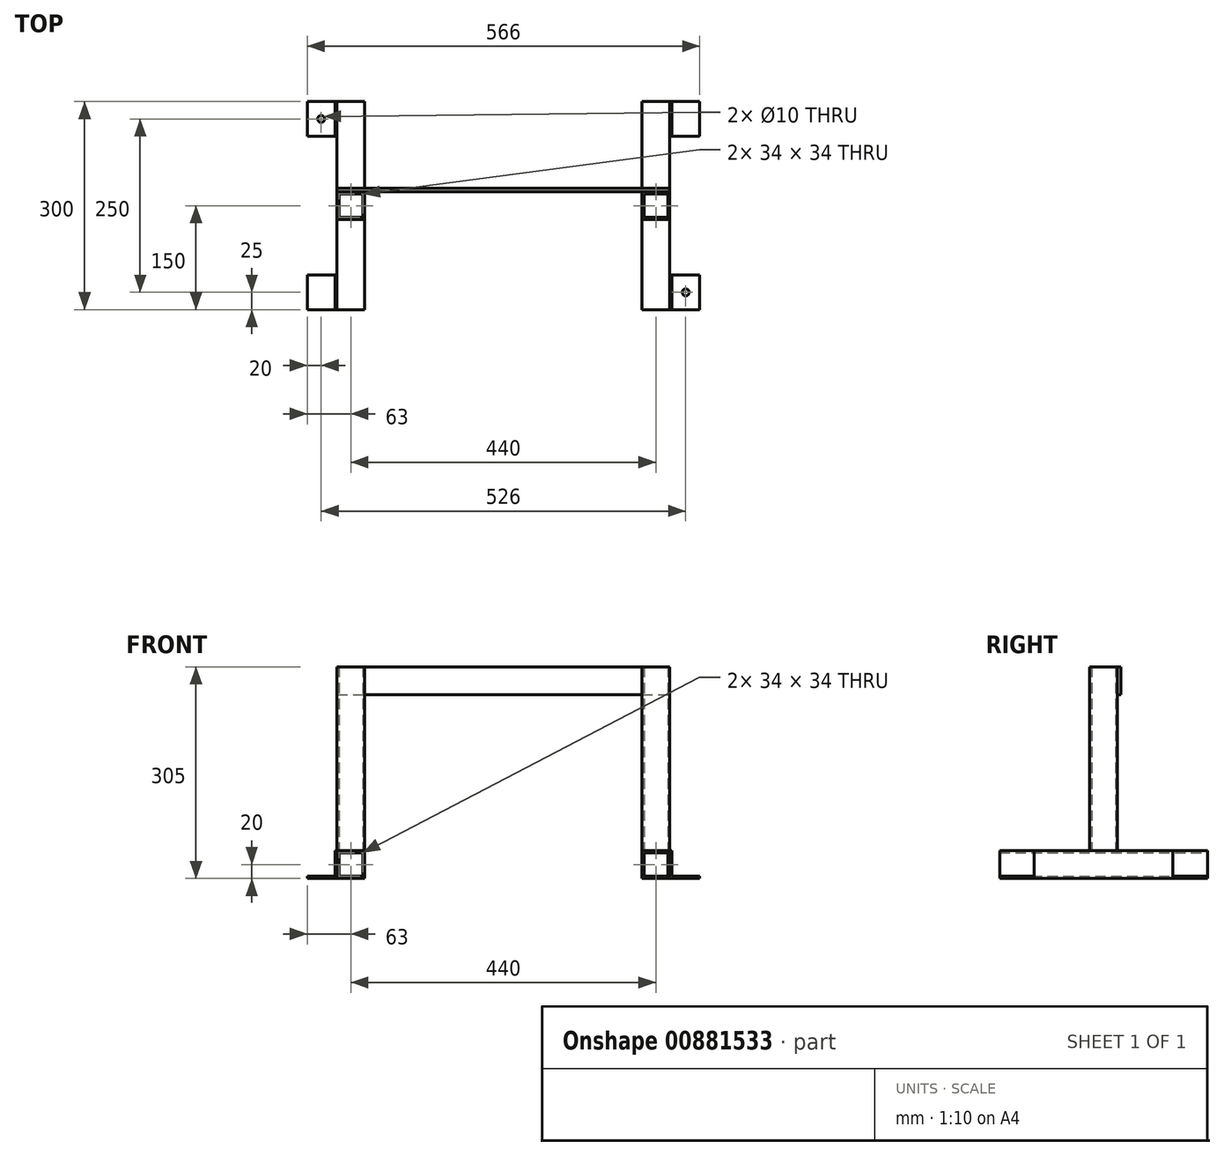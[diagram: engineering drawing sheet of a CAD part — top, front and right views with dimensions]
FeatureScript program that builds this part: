
annotation { "Feature Type Name" : "Feature", "Feature Type Description" : "" }
export const myFeature = defineFeature(function(context is Context, id is Id, definition is map)
    precondition{}
    {
        {
            var Q0;
            Q0=qCreatedBy(makeId("Front.planeOp"),FACE);
            var sketch = newSketch(context, id + "F0", { "sketchPlane" : qUnion([Q0])});
            skLineSegment(sketch, "E0", {"start": v(0, 0) * mm, "end": v(-200, 0) * mm});
            skLineSegment(sketch, "E1", {"start": v(-200, 0) * mm, "end": v(200, 0) * mm});
            skLineSegment(sketch, "E2.bottom", {"start": v(-200, 0) * mm, "end": v(-240, 0) * mm});
            skLineSegment(sketch, "E2.top", {"start": v(-200, 40) * mm, "end": v(-240, 40) * mm});
            skLineSegment(sketch, "E2.left", {"start": v(-200, 0) * mm, "end": v(-200, 40) * mm});
            skLineSegment(sketch, "E2.right", {"start": v(-240, 0) * mm, "end": v(-240, 40) * mm});
            skLineSegment(sketch, "E3", {"start": v(0, 0) * mm, "end": v(0, 28.57) * mm, "construction": true});
            skLineSegment(sketch, "E4.MirrorCS", {"start": v(200, 0) * mm, "end": v(200, 40) * mm});
            skLineSegment(sketch, "E5.MirrorCS", {"start": v(200, 40) * mm, "end": v(240, 40) * mm});
            skLineSegment(sketch, "E6.MirrorCS", {"start": v(240, 0) * mm, "end": v(240, 40) * mm});
            skLineSegment(sketch, "E7.MirrorCS", {"start": v(200, 0) * mm, "end": v(240, 0) * mm});
            skLineSegment(sketch, "E8.0", {"start": v(-237, 3) * mm, "end": v(-237, 37) * mm});
            skLineSegment(sketch, "E8.1", {"start": v(-203, 3) * mm, "end": v(-237, 3) * mm});
            skLineSegment(sketch, "E8.2", {"start": v(-203, 3) * mm, "end": v(-203, 37) * mm});
            skLineSegment(sketch, "E8.3", {"start": v(-203, 37) * mm, "end": v(-237, 37) * mm});
            skLineSegment(sketch, "E9.MirrorCS", {"start": v(203, 37) * mm, "end": v(237, 37) * mm});
            skLineSegment(sketch, "E10.MirrorCS", {"start": v(203, 3) * mm, "end": v(203, 37) * mm});
            skLineSegment(sketch, "E11.MirrorCS", {"start": v(203, 3) * mm, "end": v(237, 3) * mm});
            skLineSegment(sketch, "E12.MirrorCS", {"start": v(237, 3) * mm, "end": v(237, 37) * mm});
            skSolve(sketch);
        }
        {
            var Q0;
            Q0=qSketchRegion(id+"F0",true);
            extrude(context, id + "F1", {"entities" : qUnion([Q0]), "depth" : 300 * mm, "offsetDistance" : 25 * mm, "symmetric" : true});
        }
        {
            var Q0;
            Q0=makeQuery(id+"F1.opExtrude","SWEPT_FACE",FACE,{"disambiguationData":[OSD([sQuery(id+"F0.wireOp",EDGE,"E2.top")])]});
            var sketch = newSketch(context, id + "F2", { "sketchPlane" : qUnion([Q0])});
            skLineSegment(sketch, "E13", {"start": v(-240, 0) * mm, "end": v(-240, 20) * mm});
            skLineSegment(sketch, "E14.bottom", {"start": v(-240, 20) * mm, "end": v(-200, 20) * mm});
            skLineSegment(sketch, "E14.top", {"start": v(-240, -20) * mm, "end": v(-200, -20) * mm});
            skLineSegment(sketch, "E14.left", {"start": v(-240, 20) * mm, "end": v(-240, -20) * mm});
            skLineSegment(sketch, "E14.right", {"start": v(-200, 20) * mm, "end": v(-200, -20) * mm});
            skLineSegment(sketch, "E15.0", {"start": v(-237, 17) * mm, "end": v(-203, 17) * mm});
            skLineSegment(sketch, "E16.0", {"start": v(-237, 17) * mm, "end": v(-237, -17) * mm});
            skLineSegment(sketch, "E17.0", {"start": v(-237, -17) * mm, "end": v(-203, -17) * mm});
            skLineSegment(sketch, "E18.0", {"start": v(-203, 17) * mm, "end": v(-203, -17) * mm});
            skLineSegment(sketch, "E19", {"start": v(0, 0) * mm, "end": v(0, 43.2) * mm, "construction": true});
            skLineSegment(sketch, "E20.MirrorCS", {"start": v(200, 20) * mm, "end": v(200, -20) * mm});
            skLineSegment(sketch, "E21.MirrorCS", {"start": v(240, 20) * mm, "end": v(200, 20) * mm});
            skLineSegment(sketch, "E22.MirrorCS", {"start": v(240, 20) * mm, "end": v(240, -20) * mm});
            skLineSegment(sketch, "E23.MirrorCS", {"start": v(240, -20) * mm, "end": v(200, -20) * mm});
            skLineSegment(sketch, "E24.MirrorCS", {"start": v(237, -17) * mm, "end": v(203, -17) * mm});
            skLineSegment(sketch, "E25.MirrorCS", {"start": v(237, 17) * mm, "end": v(237, -17) * mm});
            skLineSegment(sketch, "E26.MirrorCS", {"start": v(237, 17) * mm, "end": v(203, 17) * mm});
            skLineSegment(sketch, "E27.MirrorCS", {"start": v(203, 17) * mm, "end": v(203, -17) * mm});
            skSolve(sketch);
        }
        {
            var Q0;
            Q0=qSketchRegion(id+"F2",true);
            extrude(context, id + "F3", {"entities" : qUnion([Q0]), "depth" : 265 * mm, "offsetDistance" : 25 * mm});
        }
        {
            var Q0;
            Q0=makeQuery(id+"F1.opExtrude","CAP_FACE",FACE,{"disambiguationData":[OSD([sQuery(id+"F0.wireOp",EDGE,"E2.bottom"),sQuery(id+"F0.wireOp",EDGE,"E2.top"),sQuery(id+"F0.wireOp",EDGE,"E2.left"),sQuery(id+"F0.wireOp",EDGE,"E2.right"),sQuery(id+"F0.wireOp",EDGE,"E8.0"),sQuery(id+"F0.wireOp",EDGE,"E8.1"),sQuery(id+"F0.wireOp",EDGE,"E8.2"),sQuery(id+"F0.wireOp",EDGE,"E8.3")])],"isStart":false});
            var sketch = newSketch(context, id + "F4", { "sketchPlane" : qUnion([Q0])});
            skLineSegment(sketch, "E28", {"start": v(-240, 40) * mm, "end": v(-243, 40) * mm});
            skLineSegment(sketch, "E29", {"start": v(-243, 40) * mm, "end": v(-243, 3) * mm});
            skLineSegment(sketch, "E30", {"start": v(-243, 3) * mm, "end": v(-283, 3) * mm});
            skLineSegment(sketch, "E31", {"start": v(-283, 3) * mm, "end": v(-283, 0) * mm});
            skLineSegment(sketch, "E32", {"start": v(-283, 0) * mm, "end": v(-240, 0) * mm});
            skLineSegment(sketch, "E33.MirrorCS", {"start": v(243, 3) * mm, "end": v(283, 3) * mm});
            skLineSegment(sketch, "E34.MirrorCS", {"start": v(283, 0) * mm, "end": v(240, 0) * mm});
            skLineSegment(sketch, "E35.MirrorCS", {"start": v(243, 40) * mm, "end": v(243, 3) * mm});
            skLineSegment(sketch, "E36.MirrorCS", {"start": v(240, 40) * mm, "end": v(243, 40) * mm});
            skLineSegment(sketch, "E37.MirrorCS", {"start": v(283, 3) * mm, "end": v(283, 0) * mm});
            skLineSegment(sketch, "E38", {"start": v(-240, 40) * mm, "end": v(-240, 0) * mm});
            skLineSegment(sketch, "E39.MirrorCS", {"start": v(240, 40) * mm, "end": v(240, 0) * mm});
            skSolve(sketch);
        }
        {
            var Q0;
            Q0=makeQuery(id+"F4.imprint","IMPRINT",FACE,{"disambiguationData":[TD([[makeQuery(id+"F4.imprint","IMPRINT",EDGE,{"derivedFrom":sQuery(id+"F4.wireOp",EDGE,"E28")}),1.0]])]});
            var Q1;
            Q1=makeQuery(id+"F4.imprint","IMPRINT",FACE,{"disambiguationData":[TD([[makeQuery(id+"F4.imprint","IMPRINT",EDGE,{"derivedFrom":sQuery(id+"F4.wireOp",EDGE,"E33.MirrorCS")}),-1.0]])]});
            extrude(context, id + "F5", {"entities" : qUnion([Q0, Q1]), "oppositeDirection" : true, "depth" : 50 * mm, "offsetDistance" : 25 * mm});
        }
        {
            var Q0;
            Q0=makeQuery(id+"F5.opExtrude","SWEPT_BODY",BODY,{"disambiguationData":[OSD([sQuery(id+"F4.wireOp",EDGE,"E33.MirrorCS"),sQuery(id+"F4.wireOp",EDGE,"E34.MirrorCS"),sQuery(id+"F4.wireOp",EDGE,"E35.MirrorCS"),sQuery(id+"F4.wireOp",EDGE,"E36.MirrorCS"),sQuery(id+"F4.wireOp",EDGE,"E37.MirrorCS"),sQuery(id+"F4.wireOp",EDGE,"E39.MirrorCS")])]});
            var Q1;
            Q1=qCreatedBy(makeId("Front.planeOp"),FACE);
            mirror(context, id + "F6", {"entities" : qUnion([Q0]), "mirrorPlane" : qUnion([Q1])});
        }
        {
            var Q0;
            Q0=makeQuery(id+"F1.opExtrude","CAP_FACE",FACE,{"disambiguationData":[OSD([sQuery(id+"F0.wireOp",EDGE,"E2.bottom"),sQuery(id+"F0.wireOp",EDGE,"E2.top"),sQuery(id+"F0.wireOp",EDGE,"E2.left"),sQuery(id+"F0.wireOp",EDGE,"E2.right"),sQuery(id+"F0.wireOp",EDGE,"E8.0"),sQuery(id+"F0.wireOp",EDGE,"E8.1"),sQuery(id+"F0.wireOp",EDGE,"E8.2"),sQuery(id+"F0.wireOp",EDGE,"E8.3")])],"isStart":true});
            var sketch = newSketch(context, id + "F7", { "sketchPlane" : qUnion([Q0])});
            skLineSegment(sketch, "E40.0.0", {"start": v(283, 0) * mm, "end": v(283, 3) * mm});
            skLineSegment(sketch, "E40.0.1", {"start": v(283, 3) * mm, "end": v(243, 3) * mm});
            skLineSegment(sketch, "E40.0.2", {"start": v(243, 3) * mm, "end": v(243, 40) * mm});
            skLineSegment(sketch, "E40.0.3", {"start": v(243, 40) * mm, "end": v(240, 40) * mm});
            skLineSegment(sketch, "E40.0.4", {"start": v(240, 40) * mm, "end": v(240, 0) * mm});
            skLineSegment(sketch, "E40.0.5", {"start": v(240, 0) * mm, "end": v(283, 0) * mm});
            skSolve(sketch);
        }
        {
            var Q0;
            Q0=makeQuery(id+"F7.imprint","IMPRINT",FACE,{"disambiguationData":[TD([[makeQuery(id+"F7.imprint","IMPRINT",EDGE,{"derivedFrom":sQuery(id+"F7.wireOp",EDGE,"E40.0.0")}),1.0]])]});
            extrude(context, id + "F8", {"entities" : qUnion([Q0]), "oppositeDirection" : true, "depth" : 50 * mm, "offsetDistance" : 25 * mm});
        }
        {
            var Q0;
            Q0=makeQuery(id+"F3.opExtrude","SWEPT_FACE",FACE,{"disambiguationData":[OSD([sQuery(id+"F2.wireOp",EDGE,"E14.bottom")])]});
            var sketch = newSketch(context, id + "F9", { "sketchPlane" : qUnion([Q0])});
            skLineSegment(sketch, "E41.bottom", {"start": v(240, 305) * mm, "end": v(-240, 305) * mm});
            skLineSegment(sketch, "E41.top", {"start": v(240, 265) * mm, "end": v(-240, 265) * mm});
            skLineSegment(sketch, "E41.left", {"start": v(240, 305) * mm, "end": v(240, 265) * mm});
            skLineSegment(sketch, "E41.right", {"start": v(-240, 305) * mm, "end": v(-240, 265) * mm});
            skSolve(sketch);
        }
        {
            var Q0;
            {var subQ3=sQuery(id+"F9.wireOp",EDGE,"E41.right");Q0=makeQuery(id+"F9.imprint","IMPRINT",FACE,{"disambiguationData":[TD([[makeQuery(id+"F9.imprint","IMPRINT",EDGE,{"derivedFrom":subQ3}),1.0]])]});}
            var Q1;
            {var subQ0=sQuery(id+"F9.wireOp",EDGE,"E41.left");Q1=makeQuery(id+"F9.imprint","IMPRINT",FACE,{"disambiguationData":[TD([[makeQuery(id+"F9.imprint","IMPRINT",EDGE,{"derivedFrom":subQ0}),-1.0]])]});}
            extrude(context, id + "F10", {"entities" : qUnion([Q0, Q1]), "depth" : 5 * mm, "offsetDistance" : 25 * mm});
        }
        {
            var Q0;
            Q0=makeQuery(id+"F8.opExtrude","SWEPT_FACE",FACE,{"disambiguationData":[OSD([sQuery(id+"F7.wireOp",EDGE,"E40.0.1")])]});
            var sketch = newSketch(context, id + "F11", { "sketchPlane" : qUnion([Q0])});
            skLineSegment(sketch, "E42.0.0", {"start": v(-243, 150) * mm, "end": v(-283, 150) * mm});
            skLineSegment(sketch, "E42.0.1", {"start": v(-283, 150) * mm, "end": v(-283, 100) * mm});
            skLineSegment(sketch, "E42.0.2", {"start": v(-283, 100) * mm, "end": v(-243, 100) * mm});
            skLineSegment(sketch, "E42.0.3", {"start": v(-243, 100) * mm, "end": v(-243, 150) * mm});
            skLineSegment(sketch, "E43", {"start": v(-263, 150) * mm, "end": v(-263, 100) * mm});
            skCircle(sketch, "E44", {"center": v(-263, 125) * mm, "radius": 5 * mm});
            skLineSegment(sketch, "E45", {"start": v(-263, 125) * mm, "end": v(-283, 125) * mm});
            skLineSegment(sketch, "E46", {"start": v(0, 0) * mm, "end": v(0, 58.97) * mm, "construction": true});
            skLineSegment(sketch, "E47", {"start": v(0, 0) * mm, "end": v(-42.42, 0) * mm, "construction": true});
            skCircle(sketch, "E48.MirrorC", {"center": v(263, 125) * mm, "radius": 5 * mm});
            skCircle(sketch, "E49.MirrorC", {"center": v(-263, -125) * mm, "radius": 5 * mm});
            skCircle(sketch, "E50.MirrorC", {"center": v(263, -125) * mm, "radius": 5 * mm});
            skSolve(sketch);
        }
        {
            var Q0;
            {var subQ0=sQuery(id+"F11.wireOp",EDGE,"E43");var subQ1=makeQuery(id+"F11.imprint","INTERSECT",VERTEX,{"derivedFrom":[subQ0,sQuery(id+"F11.wireOp",EDGE,"E45")]});Q0=makeQuery(id+"F11.imprint","IMPRINT",FACE,{"disambiguationData":[TD([[makeQuery(id+"F11.imprint","IMPRINT",EDGE,{"disambiguationData":[TD([[subQ1,1.0]])],"derivedFrom":subQ0}),1.0]])]});}
            var Q1;
            {var subQ0=sQuery(id+"F11.wireOp",EDGE,"E45");var subQ1=sQuery(id+"F11.wireOp",EDGE,"E43");var subQ2=makeQuery(id+"F11.imprint","INTERSECT",VERTEX,{"derivedFrom":[subQ1,subQ0]});Q1=makeQuery(id+"F11.imprint","IMPRINT",FACE,{"disambiguationData":[TD([[makeQuery(id+"F11.imprint","IMPRINT",EDGE,{"disambiguationData":[TD([[subQ2,-1.0]])],"derivedFrom":subQ1}),-1.0]])]});}
            var Q2;
            {var subQ0=sQuery(id+"F11.wireOp",EDGE,"E45");var subQ1=sQuery(id+"F11.wireOp",EDGE,"E43");var subQ2=makeQuery(id+"F11.imprint","INTERSECT",VERTEX,{"derivedFrom":[subQ1,subQ0]});Q2=makeQuery(id+"F11.imprint","IMPRINT",FACE,{"disambiguationData":[TD([[makeQuery(id+"F11.imprint","IMPRINT",EDGE,{"disambiguationData":[TD([[subQ2,1.0]])],"derivedFrom":subQ1}),-1.0]])]});}
            var Q3;
            Q3=makeQuery(id+"F11.imprint","IMPRINT",FACE,{"disambiguationData":[TD([[makeQuery(id+"F11.imprint","IMPRINT",EDGE,{"derivedFrom":sQuery(id+"F11.wireOp",EDGE,"E49.MirrorC")}),-1.0]])]});
            var Q4;
            Q4=makeQuery(id+"F11.imprint","IMPRINT",FACE,{"disambiguationData":[TD([[makeQuery(id+"F11.imprint","IMPRINT",EDGE,{"derivedFrom":sQuery(id+"F11.wireOp",EDGE,"E50.MirrorC")}),1.0]])]});
            var Q5;
            Q5=makeQuery(id+"F11.imprint","IMPRINT",FACE,{"disambiguationData":[TD([[makeQuery(id+"F11.imprint","IMPRINT",EDGE,{"derivedFrom":sQuery(id+"F11.wireOp",EDGE,"E48.MirrorC")}),-1.0]])]});
            extrude(context, id + "F12", {"entities" : qUnion([Q0, Q1, Q2, Q3, Q4, Q5]), "operationType" : NewBodyOperationType.REMOVE, "oppositeDirection" : true, "depth" : 25 * mm, "offsetDistance" : 25 * mm});
        }
    });
